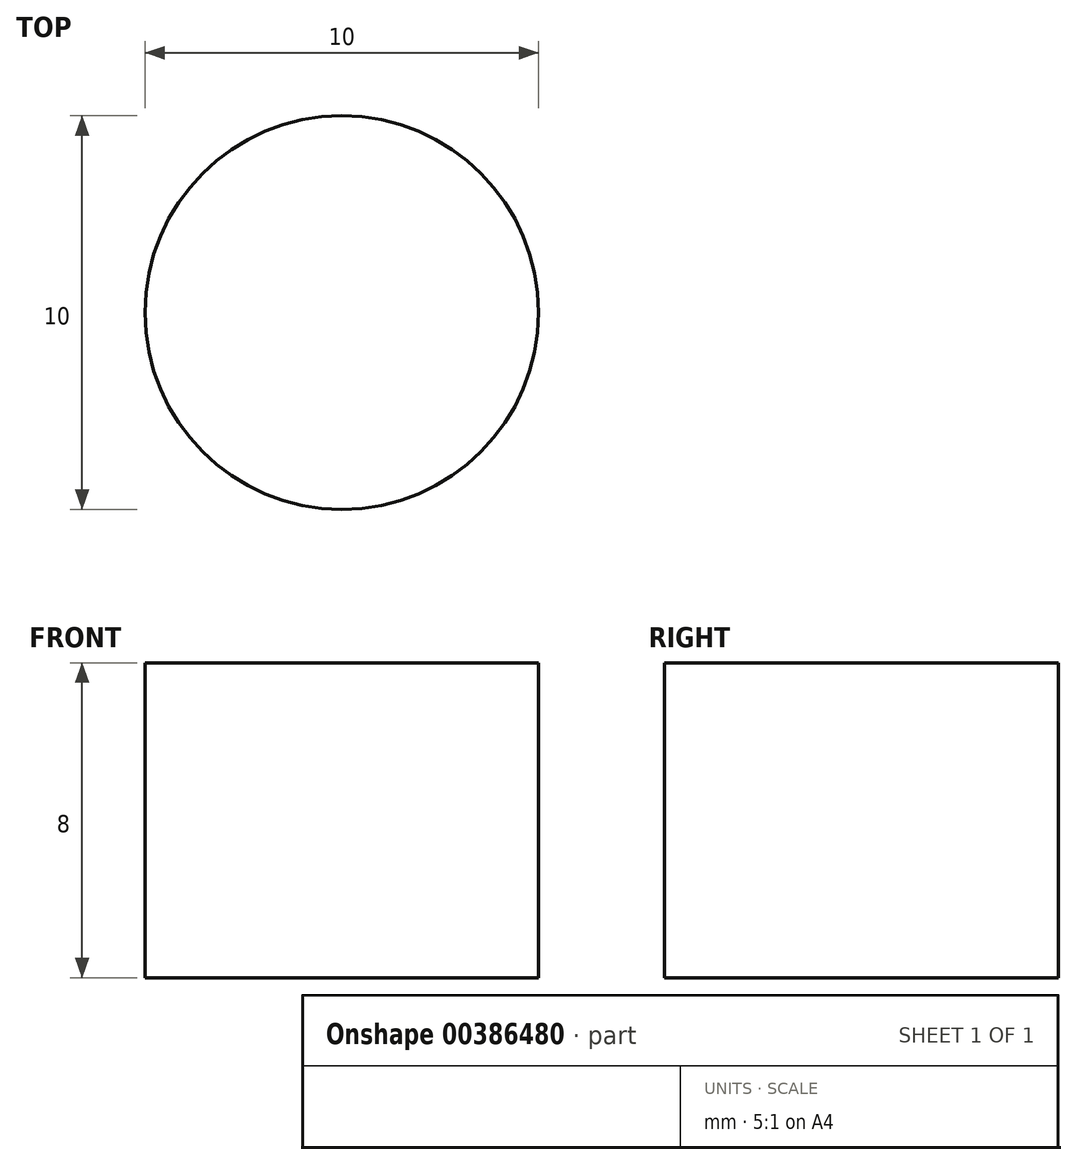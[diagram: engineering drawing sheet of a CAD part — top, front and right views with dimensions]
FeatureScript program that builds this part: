
annotation { "Feature Type Name" : "Feature", "Feature Type Description" : "" }
export const myFeature = defineFeature(function(context is Context, id is Id, definition is map)
    precondition{}
    {
        {
            var Q0;
            Q0=qCreatedBy(makeId("Top.planeOp"),FACE);
            var sketch = newSketch(context, id + "F0", { "sketchPlane" : qUnion([Q0])});
            skCircle(sketch, "E0", {"center": v(0, 0) * mm, "radius": 5 * mm});
            skSolve(sketch);
        }
        {
            var Q0;
            Q0=makeQuery(id+"F0.imprint","IMPRINT",FACE,{"disambiguationData":[TD([[makeQuery(id+"F0.imprint","IMPRINT",EDGE,{"derivedFrom":sQuery(id+"F0.wireOp",EDGE,"E0")}),1.0]])]});
            extrude(context, id + "F1", {"entities" : qUnion([Q0]), "depth" : 8 * mm});
        }
    });
